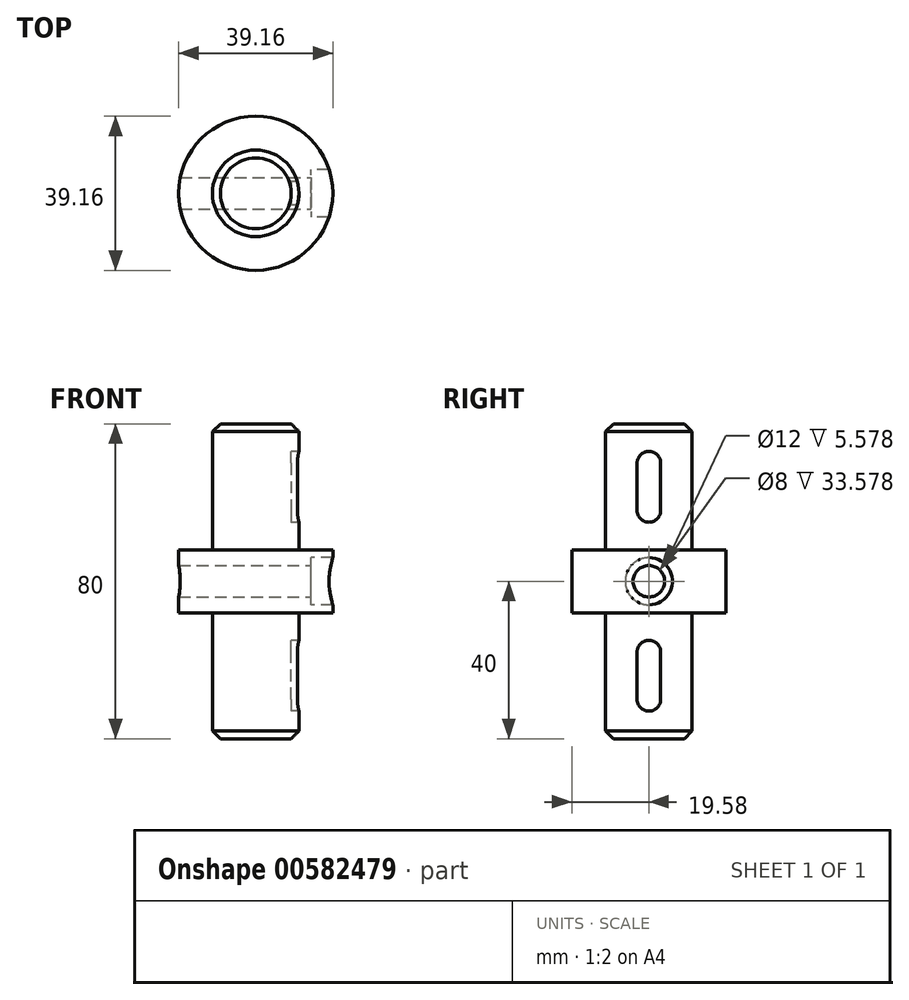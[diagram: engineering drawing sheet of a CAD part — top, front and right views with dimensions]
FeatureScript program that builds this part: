
annotation { "Feature Type Name" : "Feature", "Feature Type Description" : "" }
export const myFeature = defineFeature(function(context is Context, id is Id, definition is map)
    precondition{}
    {
        {
            var Q0;
            Q0=qCreatedBy(makeId("Top.planeOp"),FACE);
            var sketch = newSketch(context, id + "F0", { "sketchPlane" : qUnion([Q0])});
            skCircle(sketch, "E0", {"center": v(0, 0) * mm, "radius": 11 * mm});
            skSolve(sketch);
        }
        {
            var Q0;
            Q0 = qSketchRegion(id + "F0", true);
            extrude(context, id + "F1", {"entities" : qUnion([Q0]), "endBound" : BoundingType.SYMMETRIC, "depth" : 80 * mm, "offsetDistance" : 25 * mm});
        }
        {
            var Q0;
            Q0=makeQuery(id+"F1.opExtrude","CAP_FACE",FACE,{"disambiguationData":[OSD([sQuery(id+"F0.wireOp",EDGE,"E0")])],"isStart":false});
            var sketch = newSketch(context, id + "F2", { "sketchPlane" : qUnion([Q0])});
            skCircle(sketch, "E1", {"center": v(0, 0) * mm, "radius": 11 * mm});
            skSolve(sketch);
        }
        {
            var Q0;
            Q0=makeQuery(id+"F1.opExtrude","CAP_FACE",FACE,{"disambiguationData":[OSD([sQuery(id+"F0.wireOp",EDGE,"E0")])],"isStart":false});
            chamfer(context, id + "F3", {"entities" : qUnion([Q0]), "width" : 2 * mm, "tangentPropagation" : true});
        }
        {
            var Q0;
            Q0=makeQuery(id+"F1.opExtrude","CAP_EDGE",EDGE,{"disambiguationData":[OSD([sQuery(id+"F0.wireOp",EDGE,"E0")])],"isStart":true});
            chamfer(context, id + "F4", {"entities" : qUnion([Q0]), "width" : 2 * mm, "tangentPropagation" : true});
        }
        {
            var Q0;
            Q0=qCreatedBy(makeId("Top.planeOp"),FACE);
            var sketch = newSketch(context, id + "F5", { "sketchPlane" : qUnion([Q0])});
            skCircle(sketch, "E2", {"center": v(0, 0) * mm, "radius": 19.58 * mm});
            skSolve(sketch);
        }
        {
            var Q0;
            Q0 = qSketchRegion(id + "F5", true);
            extrude(context, id + "F6", {"entities" : qUnion([Q0]), "operationType" : NewBodyOperationType.ADD, "endBound" : BoundingType.SYMMETRIC, "depth" : 16 * mm, "offsetDistance" : 25 * mm});
        }
        {
            var Q0;
            Q0=qCreatedBy(makeId("Right.planeOp"),FACE);
            cPlane(context, id + "F7", {"entities" : qUnion([Q0]), "cplaneType" : CPlaneType.OFFSET, "offset" : 14 * mm, "width" : 150 * mm, "height" : 150 * mm});
        }
        {
            var Q0;
            Q0=qCreatedBy(id+"F7.planeOp",FACE);
            var sketch = newSketch(context, id + "F8", { "sketchPlane" : qUnion([Q0])});
            skCircle(sketch, "E3", {"center": v(0, 0) * mm, "radius": 6 * mm});
            skSolve(sketch);
        }
        {
            var Q0;
            Q0 = qSketchRegion(id + "F8", true);
            extrude(context, id + "F9", {"entities" : qUnion([Q0]), "operationType" : NewBodyOperationType.REMOVE, "depth" : 30 * mm, "offsetDistance" : 25 * mm});
        }
        {
            var Q0;
            Q0=qCreatedBy(makeId("Right.planeOp"),FACE);
            cPlane(context, id + "F10", {"entities" : qUnion([Q0]), "cplaneType" : CPlaneType.OFFSET, "offset" : 9 * mm, "width" : 150 * mm, "height" : 150 * mm});
        }
        {
            var Q0;
            Q0=qCreatedBy(id+"F7.planeOp",FACE);
            var sketch = newSketch(context, id + "F11", { "sketchPlane" : qUnion([Q0])});
            skCircle(sketch, "E4", {"center": v(0, 0) * mm, "radius": 4 * mm});
            skSolve(sketch);
        }
        {
            var Q0;
            Q0 = qSketchRegion(id + "F11", true);
            extrude(context, id + "F12", {"entities" : qUnion([Q0]), "operationType" : NewBodyOperationType.REMOVE, "endBound" : BoundingType.THROUGH_ALL, "oppositeDirection" : true, "depth" : 25 * mm, "offsetDistance" : 25 * mm});
        }
        {
            var Q0;
            Q0=qCreatedBy(makeId("Right.planeOp"),FACE);
            cPlane(context, id + "F13", {"entities" : qUnion([Q0]), "cplaneType" : CPlaneType.OFFSET, "offset" : 9 * mm, "width" : 150 * mm, "height" : 150 * mm});
        }
        {
            var Q0;
            Q0=qCreatedBy(id+"F13.planeOp",FACE);
            var sketch = newSketch(context, id + "F14", { "sketchPlane" : qUnion([Q0])});
            skLineSegment(sketch, "E5", {"start": v(3, 30) * mm, "end": v(3, 18) * mm});
            skLineSegment(sketch, "E6", {"start": v(-3, 30) * mm, "end": v(-3, 18) * mm});
            skArc(sketch, "E7", {"start": v(3, 30) * mm, "mid": v(0, 33) * mm, "end": v(-3, 30) * mm});
            skArc(sketch, "E8", {"start": v(-3, 18) * mm, "mid": v(0, 15) * mm, "end": v(3, 18) * mm});
            skSolve(sketch);
        }
        {
            var Q0;
            Q0 = qSketchRegion(id + "F14", true);
            extrude(context, id + "F15", {"entities" : qUnion([Q0]), "operationType" : NewBodyOperationType.REMOVE, "endBound" : BoundingType.THROUGH_ALL, "depth" : 25 * mm, "offsetDistance" : 25 * mm});
        }
        {
            var Q0;
            Q0=qCreatedBy(id+"F10.planeOp",FACE);
            var sketch = newSketch(context, id + "F16", { "sketchPlane" : qUnion([Q0])});
            skLineSegment(sketch, "E9", {"start": v(-3, -30) * mm, "end": v(-3, -18) * mm});
            skLineSegment(sketch, "E10", {"start": v(3, -30) * mm, "end": v(3, -18) * mm});
            skArc(sketch, "E11", {"start": v(-3, -30) * mm, "mid": v(0, -33) * mm, "end": v(3, -30) * mm});
            skArc(sketch, "E12", {"start": v(3, -18) * mm, "mid": v(0, -15) * mm, "end": v(-3, -18) * mm});
            skSolve(sketch);
        }
        {
            var Q0;
            Q0 = qSketchRegion(id + "F16", true);
            extrude(context, id + "F17", {"entities" : qUnion([Q0]), "operationType" : NewBodyOperationType.REMOVE, "depth" : 25 * mm, "offsetDistance" : 25 * mm});
        }
    });
